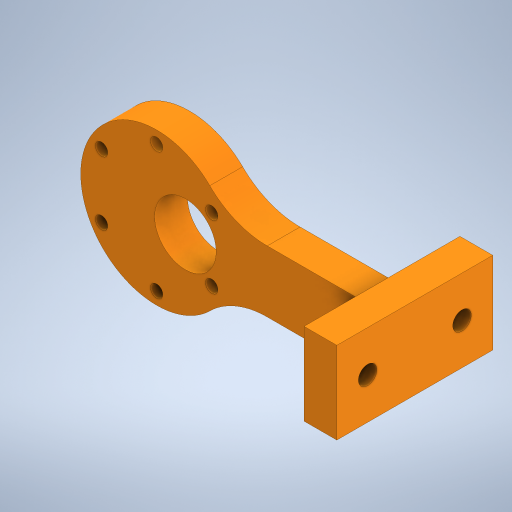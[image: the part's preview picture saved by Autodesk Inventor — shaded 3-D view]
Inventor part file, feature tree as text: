
AUTODESK INVENTOR PART (.ipt)
format: ipt  version: 2023 (Build 270158000, 158)  size: 281,600 bytes
history: native  units: mm
features: other x3, extrude x2, sketch x2, fillet x1, reference x1
ambient origin geometry x8: Origin, YZ Plane, XZ Plane, XY Plane, X Axis, Y Axis, Z Axis, Center Point
bodies: Solid1 (feature_tree)
feature tree (9):
  extrude  "Extrusion1"  Depth=15.0mm
  extrude  "Extrusion2"  Depth=7.0mm
  fillet  "Fillet1"  Radius=2.5mm
  sketch  "Sketch1"  dims[d0=15.0mm d1=35.0mm]
  reference  "Reference1"
  sketch  "Sketch2"  dims[d2=20.0mm d3=7.0mm d4=2.5mm d5=0.0mm d6=8.0mm d7=0.0mm d8=20.0mm d9=0.0mm d10=38.0mm d11=15.0mm d12=4.5mm d13=4.5mm d14=7.5mm d15=7.5mm d16=8.0mm d17=0.0mm d18=20.0mm]
  other  "<userpath>\OneDrive\Objet3D\3DPrinter\3DPrinterBeltCoreXY.iam"
  other  "3DPrinterBeltCoreXY.iam"
  other  "DCMotor:1"
